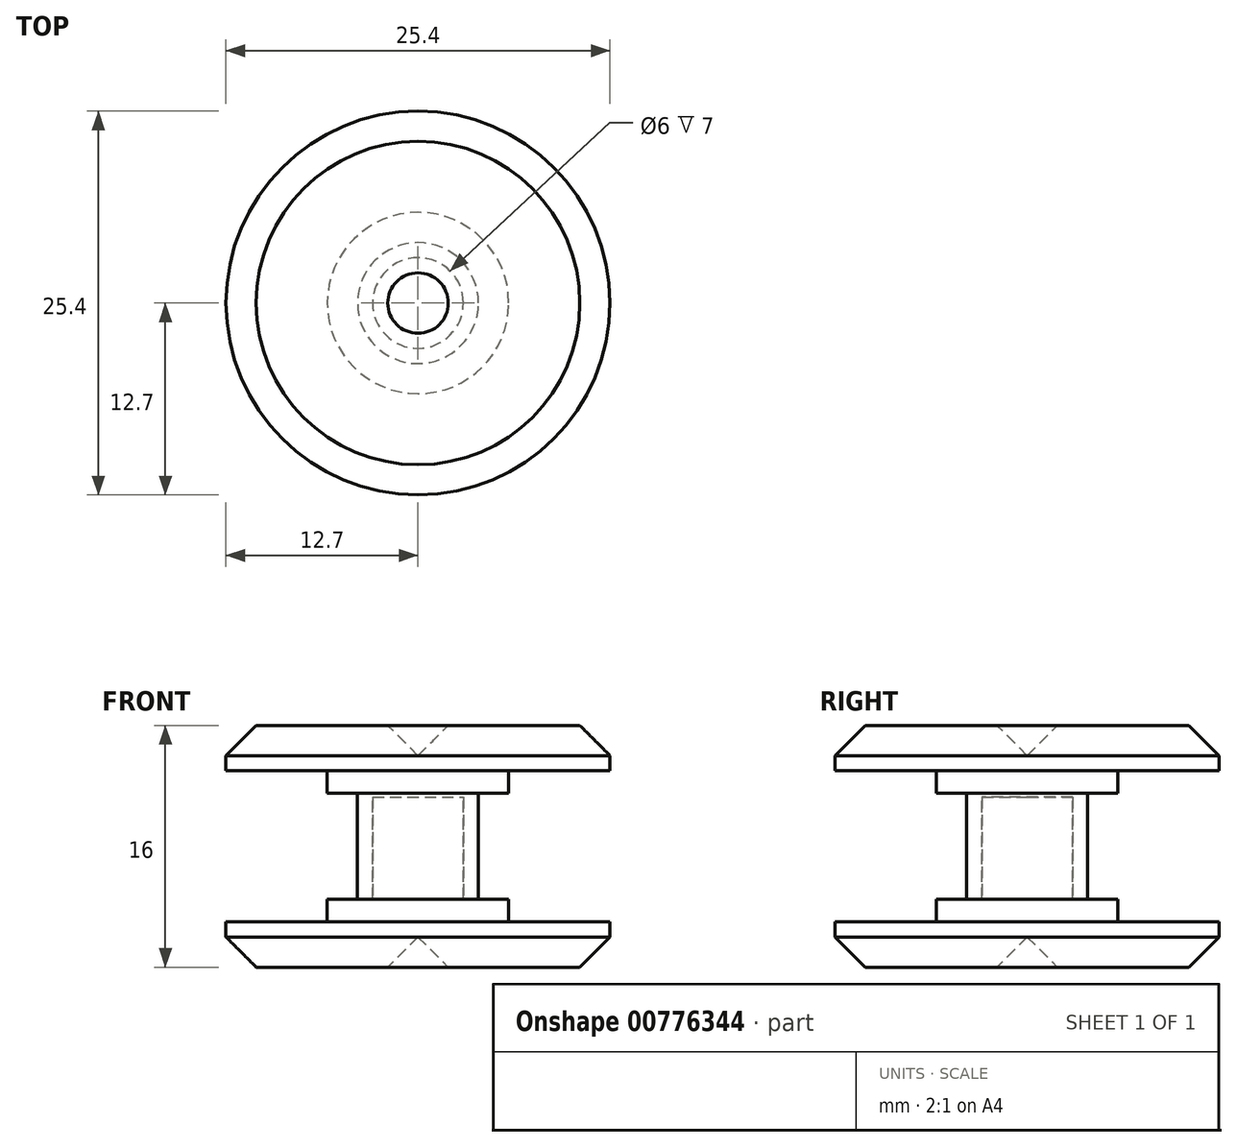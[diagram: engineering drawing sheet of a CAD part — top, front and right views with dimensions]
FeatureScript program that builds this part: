
annotation { "Feature Type Name" : "Feature", "Feature Type Description" : "" }
export const myFeature = defineFeature(function(context is Context, id is Id, definition is map)
    precondition{}
    {
        {
            var Q0;
            Q0=qCreatedBy(makeId("Front.planeOp"),FACE);
            var sketch = newSketch(context, id + "F0", { "sketchPlane" : qUnion([Q0])});
            skLineSegment(sketch, "E0", {"start": v(0, 7) * mm, "end": v(3, 7) * mm});
            skLineSegment(sketch, "E1", {"start": v(3, 7) * mm, "end": v(3, 0) * mm});
            skLineSegment(sketch, "E2", {"start": v(3, 0) * mm, "end": v(4, 0) * mm});
            skLineSegment(sketch, "E3", {"start": v(4, 0) * mm, "end": v(4, 7) * mm});
            skLineSegment(sketch, "E4", {"start": v(4, 7) * mm, "end": v(6, 7) * mm});
            skLineSegment(sketch, "E5", {"start": v(12.7, 8.5) * mm, "end": v(12.7, 9.5) * mm});
            skLineSegment(sketch, "E6", {"start": v(12.7, 9.5) * mm, "end": v(10.7, 11.5) * mm});
            skLineSegment(sketch, "E7", {"start": v(0, 9.5) * mm, "end": v(0, 7) * mm});
            skLineSegment(sketch, "E8", {"start": v(6, 7) * mm, "end": v(6, 8.5) * mm});
            skLineSegment(sketch, "E9", {"start": v(6, 8.5) * mm, "end": v(12.7, 8.5) * mm});
            skLineSegment(sketch, "E10", {"start": v(10.7, 11.5) * mm, "end": v(2, 11.5) * mm});
            skLineSegment(sketch, "E11", {"start": v(2, 11.5) * mm, "end": v(0, 9.5) * mm});
            skSolve(sketch);
        }
        {
            var Q0;
            Q0=makeQuery(id+"F0.imprint","IMPRINT",FACE,{"disambiguationData":[TD([[makeQuery(id+"F0.imprint","IMPRINT",EDGE,{"derivedFrom":sQuery(id+"F0.wireOp",EDGE,"E0")}),1.0]])]});
            var Q1;
            Q1=sQuery(id+"F0.wireOp",EDGE,"E7");
            revolve(context, id + "F1", {"surfaceOperationType" : NewSurfaceOperationType.NEW, "entities" : qUnion([Q0]), "axis" : qUnion([Q1]), "revolveType" : RevolveType.FULL});
        }
        {
            var Q0;
            Q0=qCreatedBy(makeId("Front.planeOp"),FACE);
            var sketch = newSketch(context, id + "F2", { "sketchPlane" : qUnion([Q0])});
            skLineSegment(sketch, "E12", {"start": v(0, -2.5) * mm, "end": v(0, 6.75) * mm});
            skLineSegment(sketch, "E13", {"start": v(0, 6.75) * mm, "end": v(3, 6.75) * mm});
            skLineSegment(sketch, "E14", {"start": v(3, 6.75) * mm, "end": v(3, 0) * mm});
            skLineSegment(sketch, "E15", {"start": v(3, 0) * mm, "end": v(6, 0) * mm});
            skLineSegment(sketch, "E16", {"start": v(6, 0) * mm, "end": v(6, -1.5) * mm});
            skLineSegment(sketch, "E17", {"start": v(6, -1.5) * mm, "end": v(12.7, -1.5) * mm});
            skLineSegment(sketch, "E18", {"start": v(12.7, -1.5) * mm, "end": v(12.7, -2.5) * mm});
            skLineSegment(sketch, "E19", {"start": v(12.7, -2.5) * mm, "end": v(10.7, -4.5) * mm});
            skLineSegment(sketch, "E20", {"start": v(10.7, -4.5) * mm, "end": v(2, -4.5) * mm});
            skLineSegment(sketch, "E21", {"start": v(2, -4.5) * mm, "end": v(0, -2.5) * mm});
            skSolve(sketch);
        }
        {
            var Q0;
            Q0=makeQuery(id+"F2.imprint","IMPRINT",FACE,{"disambiguationData":[TD([[makeQuery(id+"F2.imprint","IMPRINT",EDGE,{"derivedFrom":sQuery(id+"F2.wireOp",EDGE,"E12")}),-1.0]])]});
            var Q1;
            Q1=sQuery(id+"F2.wireOp",EDGE,"E12");
            revolve(context, id + "F3", {"surfaceOperationType" : NewSurfaceOperationType.NEW, "entities" : qUnion([Q0]), "axis" : qUnion([Q1]), "revolveType" : RevolveType.FULL});
        }
    });
